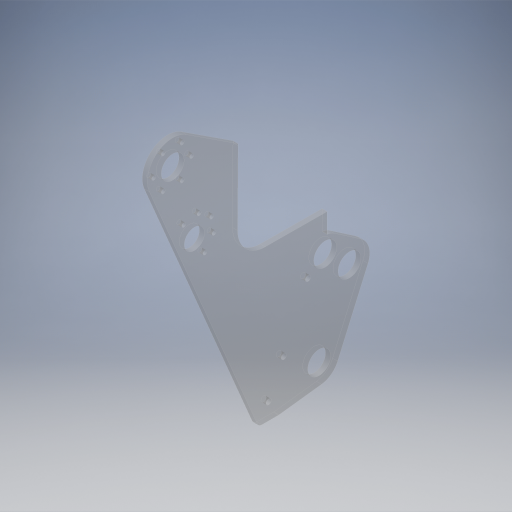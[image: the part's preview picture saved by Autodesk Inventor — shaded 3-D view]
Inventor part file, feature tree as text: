
AUTODESK INVENTOR PART (.ipt)
format: ipt  version: 2024.2 (Build 282272000, 272)  size: 483,840 bytes
history: native  units: in
note: dims shown in document units (in); Inventor stores cm internally (conversion verified against a paired STEP export)
features: sketch x10, extrude x10, projected_geometry x3, other x1
ambient origin geometry x8: Origin, YZ Plane, XZ Plane, XY Plane, X Axis, Y Axis, Z Axis, Center Point
bodies: Solid1 (feature_tree)
feature tree (24):
  sketch  "Sketch1"  dims[d0=1.875in d2=0.1969in]
  extrude  "Extrusion1"  Depth=0.1969in
  extrude  "Extrusion2"  Depth=1.0in TaperAngle=0.0deg
  extrude  "Extrusion3"  Depth=1.0in TaperAngle=0.0deg
  sketch  "Sketch4"  dims[d15=1.0in d16=0.0in d19=3.1496in d21=360.0deg]
  extrude  "Extrusion7"  Depth=1.0in TaperAngle=360.0deg
  extrude  "Extrusion8"  Depth=0.25in
  extrude  "Extrusion9"  Depth=0.25in TaperAngle=0.0deg
  sketch  "Sketch9"  dims[d32=0.25in d33=0.0in d34=0.25in d35=0.0in]
  sketch  "Sketch10"  dims[d36=0.25in d37=0.0in d8=1.9685in]
  extrude  "Extrusion10"  Depth=14.8479in
  extrude  "Extrusion11"  Depth=0.25in TaperAngle=0.0deg
  extrude  "Extrusion12"  Depth=0.25in
  extrude  "Extrusion5"  [1 undecoded]
  sketch  "Sketch2"  dims[d3=0.3937in d4=0.0in d5=1.0in d6=0.0in]
  projected_geometry  "Projected Loop1"
  sketch  "Sketch3"  dims[d7=2.3622in d9=360.0deg d11=1.0in d12=0.0in]
  sketch  "Sketch6"  dims[d23=0.25in d24=0.0in d25=0.125in]
  projected_geometry  "Projected Loop2"
  sketch  "Sketch7"  dims[d26=0.25in d27=0.0in d28=0.25in d29=0.0in]
  projected_geometry  "Projected Loop3"
  sketch  "Sketch8"  dims[d30=11.4128in d31=14.8479in]
  sketch  "Sketch11"
  other  "Part 1"
note: 1 required parameter value undecoded (feature->parameter linkage not recoverable at this tier; creation-order binding heuristic only, values carry confidence <= 0.55)
